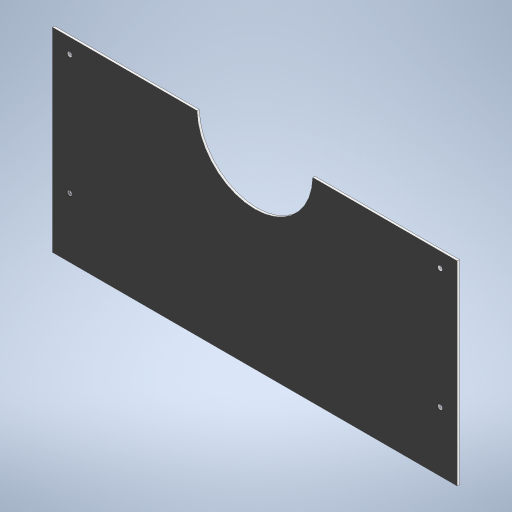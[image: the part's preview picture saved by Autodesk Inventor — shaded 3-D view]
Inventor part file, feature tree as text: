
AUTODESK INVENTOR PART (.ipt)
format: ipt  version: 2023 (Build 270158000, 158)  size: 233,472 bytes
history: native  units: mm
features: sketch x2, extrude x1, hole x1
ambient origin geometry x8: Origin, YZ Plane, XZ Plane, XY Plane, X Axis, Y Axis, Z Axis, Center Point
bodies: Solid1 (feature_tree)
feature tree (4):
  extrude  "Extrusion1"  Depth=3.0mm TaperAngle=0.0deg
  hole  "Hole1"  [1 undecoded]
  sketch  "Sketch1"  dims[d0=542.0mm d2=3.0mm d3=0.0mm]
  sketch  "Sketch2"  dims[d4=23.0mm d6=6.5mm d7=6.0mm d8=4.0mm d9=2.0mm d10=90.0deg d11=8.0mm d12=20.594885mm d13=20.0mm d14=261.0mm d15=542.0mm d16=20.0mm d18=161.0mm d19=20.0mm d21=496.0mm d24=155.0mm d25=263.0mm d26=261.0mm]
note: 1 required parameter value undecoded (feature->parameter linkage not recoverable at this tier; creation-order binding heuristic only, values carry confidence <= 0.55)
